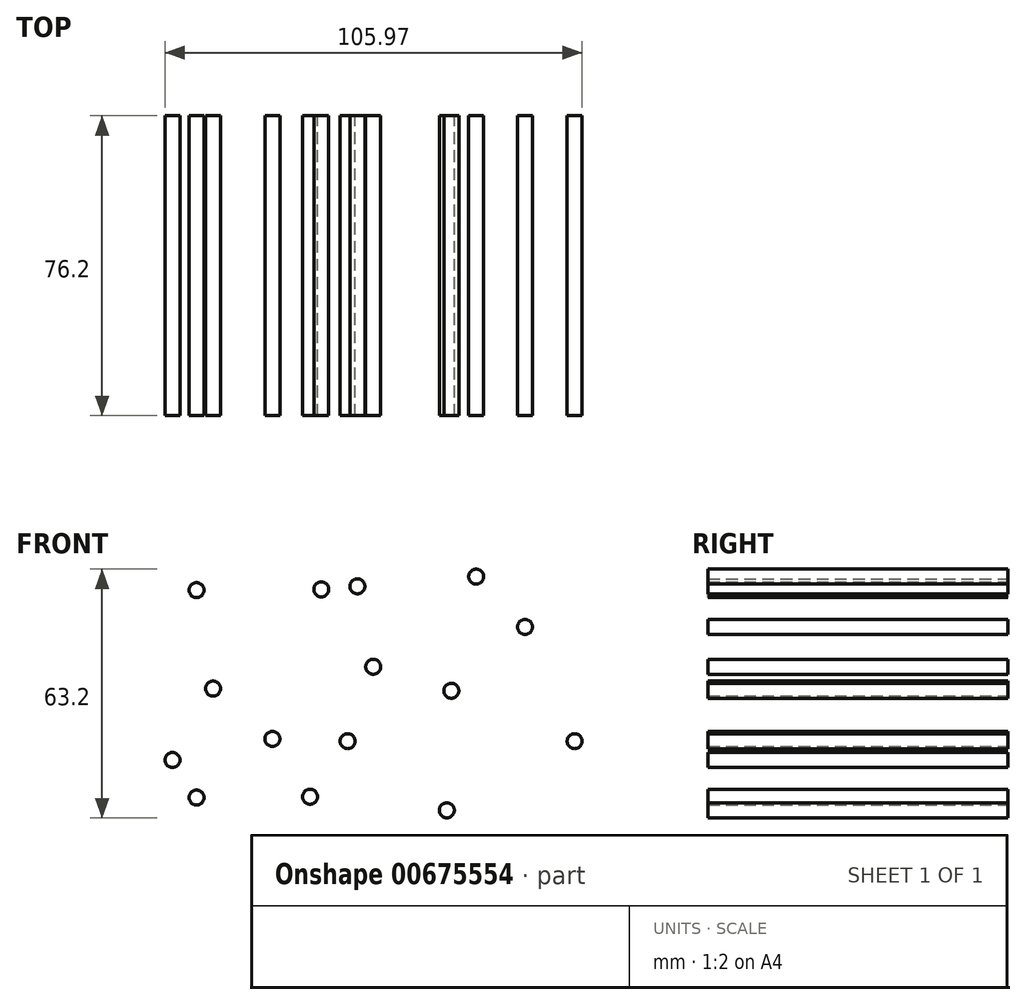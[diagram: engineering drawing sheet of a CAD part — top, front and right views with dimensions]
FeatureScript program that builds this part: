
annotation { "Feature Type Name" : "Feature", "Feature Type Description" : "" }
export const myFeature = defineFeature(function(context is Context, id is Id, definition is map)
    precondition{}
    {
        {
            var Q0;
            Q0=qCreatedBy(makeId("Front.planeOp"),FACE);
            var sketch = newSketch(context, id + "F0", { "sketchPlane" : qUnion([Q0])});
            skCircle(sketch, "E0", {"center": v(-55.85, 48.22) * mm, "radius": 1.9 * mm});
            skCircle(sketch, "E1", {"center": v(-24.16, 48.4) * mm, "radius": 1.9 * mm});
            skCircle(sketch, "E2", {"center": v(-14.99, 49.17) * mm, "radius": 1.9 * mm});
            skCircle(sketch, "E3", {"center": v(-51.65, 23.2) * mm, "radius": 1.9 * mm});
            skCircle(sketch, "E4", {"center": v(-10.98, 28.74) * mm, "radius": 1.9 * mm});
            skCircle(sketch, "E5", {"center": v(-36.57, 10.4) * mm, "radius": 1.9 * mm});
            skCircle(sketch, "E6", {"center": v(-17.47, 9.83) * mm, "radius": 1.9 * mm});
            skCircle(sketch, "E7", {"center": v(8.88, 22.63) * mm, "radius": 1.9 * mm});
            skCircle(sketch, "E8", {"center": v(27.6, 38.86) * mm, "radius": 1.9 * mm});
            skCircle(sketch, "E9", {"center": v(15.18, 51.65) * mm, "radius": 1.9 * mm});
            skCircle(sketch, "E10", {"center": v(-61.96, 5.06) * mm, "radius": 1.9 * mm});
            skCircle(sketch, "E11", {"center": v(-55.85, -4.49) * mm, "radius": 1.9 * mm});
            skCircle(sketch, "E12", {"center": v(-27.02, -4.3) * mm, "radius": 1.9 * mm});
            skCircle(sketch, "E13", {"center": v(7.73, -7.73) * mm, "radius": 1.9 * mm});
            skCircle(sketch, "E14", {"center": v(40.2, 9.83) * mm, "radius": 1.9 * mm});
            skSolve(sketch);
        }
        {
            var Q0;
            Q0=makeQuery(id+"F0.imprint","IMPRINT",FACE,{"disambiguationData":[TD([[makeQuery(id+"F0.imprint","IMPRINT",EDGE,{"derivedFrom":sQuery(id+"F0.wireOp",EDGE,"E6")}),1.0]])]});
            var Q1;
            Q1=makeQuery(id+"F0.imprint","IMPRINT",FACE,{"disambiguationData":[TD([[makeQuery(id+"F0.imprint","IMPRINT",EDGE,{"derivedFrom":sQuery(id+"F0.wireOp",EDGE,"E4")}),1.0]])]});
            var Q2;
            Q2=makeQuery(id+"F0.imprint","IMPRINT",FACE,{"disambiguationData":[TD([[makeQuery(id+"F0.imprint","IMPRINT",EDGE,{"derivedFrom":sQuery(id+"F0.wireOp",EDGE,"E2")}),1.0]])]});
            var Q3;
            Q3=makeQuery(id+"F0.imprint","IMPRINT",FACE,{"disambiguationData":[TD([[makeQuery(id+"F0.imprint","IMPRINT",EDGE,{"derivedFrom":sQuery(id+"F0.wireOp",EDGE,"E1")}),1.0]])]});
            var Q4;
            Q4=makeQuery(id+"F0.imprint","IMPRINT",FACE,{"disambiguationData":[TD([[makeQuery(id+"F0.imprint","IMPRINT",EDGE,{"derivedFrom":sQuery(id+"F0.wireOp",EDGE,"E0")}),1.0]])]});
            var Q5;
            Q5=makeQuery(id+"F0.imprint","IMPRINT",FACE,{"disambiguationData":[TD([[makeQuery(id+"F0.imprint","IMPRINT",EDGE,{"derivedFrom":sQuery(id+"F0.wireOp",EDGE,"E3")}),1.0]])]});
            var Q6;
            Q6=makeQuery(id+"F0.imprint","IMPRINT",FACE,{"disambiguationData":[TD([[makeQuery(id+"F0.imprint","IMPRINT",EDGE,{"derivedFrom":sQuery(id+"F0.wireOp",EDGE,"E10")}),1.0]])]});
            var Q7;
            Q7=makeQuery(id+"F0.imprint","IMPRINT",FACE,{"disambiguationData":[TD([[makeQuery(id+"F0.imprint","IMPRINT",EDGE,{"derivedFrom":sQuery(id+"F0.wireOp",EDGE,"E11")}),1.0]])]});
            var Q8;
            Q8=makeQuery(id+"F0.imprint","IMPRINT",FACE,{"disambiguationData":[TD([[makeQuery(id+"F0.imprint","IMPRINT",EDGE,{"derivedFrom":sQuery(id+"F0.wireOp",EDGE,"E5")}),1.0]])]});
            var Q9;
            Q9=makeQuery(id+"F0.imprint","IMPRINT",FACE,{"disambiguationData":[TD([[makeQuery(id+"F0.imprint","IMPRINT",EDGE,{"derivedFrom":sQuery(id+"F0.wireOp",EDGE,"E12")}),1.0]])]});
            var Q10;
            Q10=makeQuery(id+"F0.imprint","IMPRINT",FACE,{"disambiguationData":[TD([[makeQuery(id+"F0.imprint","IMPRINT",EDGE,{"derivedFrom":sQuery(id+"F0.wireOp",EDGE,"E13")}),1.0]])]});
            var Q11;
            Q11=makeQuery(id+"F0.imprint","IMPRINT",FACE,{"disambiguationData":[TD([[makeQuery(id+"F0.imprint","IMPRINT",EDGE,{"derivedFrom":sQuery(id+"F0.wireOp",EDGE,"E7")}),1.0]])]});
            var Q12;
            Q12=makeQuery(id+"F0.imprint","IMPRINT",FACE,{"disambiguationData":[TD([[makeQuery(id+"F0.imprint","IMPRINT",EDGE,{"derivedFrom":sQuery(id+"F0.wireOp",EDGE,"E9")}),1.0]])]});
            var Q13;
            Q13=makeQuery(id+"F0.imprint","IMPRINT",FACE,{"disambiguationData":[TD([[makeQuery(id+"F0.imprint","IMPRINT",EDGE,{"derivedFrom":sQuery(id+"F0.wireOp",EDGE,"E8")}),1.0]])]});
            var Q14;
            Q14=makeQuery(id+"F0.imprint","IMPRINT",FACE,{"disambiguationData":[TD([[makeQuery(id+"F0.imprint","IMPRINT",EDGE,{"derivedFrom":sQuery(id+"F0.wireOp",EDGE,"E14")}),1.0]])]});
            extrude(context, id + "F1", {"entities" : qUnion([Q0, Q1, Q2, Q3, Q4, Q5, Q6, Q7, Q8, Q9, Q10, Q11, Q12, Q13, Q14]), "depth" : 76.2 * mm, "offsetDistance" : 25.4 * mm});
        }
    });
